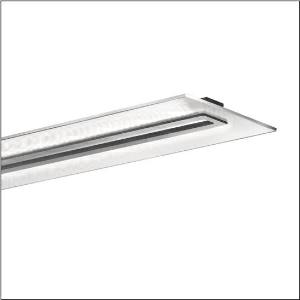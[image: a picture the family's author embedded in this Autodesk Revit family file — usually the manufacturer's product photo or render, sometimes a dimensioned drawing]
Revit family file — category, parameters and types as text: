
# Revit family: vega_r__11_5mn238dlc_e876
name_source: partatom
category: Lighting Fixtures
units: mm (PartAtom-declared; Revit-internal decimal feet)

## family parameters
Cut with Voids When Loaded = No
Host = Face
Light Source = No
Part Type = Normal
Room Calculation Point = No
Round Connector Dimension = Use Diameter
Shared = No

## types (1)
- --- (1 x LED 4000K / CRI = 80 (unbekannt), 4300 lm, 4000K)
    Apparent Load = 31 VA
    CIE Flux Codes = 61 86 97 62 100
    Color Rendering = 80
    Color Temperature = 4000K
    Default Elevation = 1800 mm
    Description = Vega® 11, office luminaire, primary light control with prismatic reflector, of PMMA, transparent prismatic structure, CAT 2 (L<= 1500cd/m²), light emission: direct/indirect distribution, primary light characteristic: symmetric, installation type: suspended mounting, surface-mounted, LED, rated luminous flux: 4.300lm, luminous efficacy: 139lm/W, light colour: 840, colour temperature: 4000K, control gear: ECG, with terminal, 3+2-pole, max. 2.5mm², mains connection: 230V, AC, 50Hz, connection cable inclusive, cable length: 1,5m, rated input power: 31W, luminaire housing, rectangular, rounded, of aluminium section, anodised, metallic grey (RAL 9006), length: 1.250mm, width: 350mm, height: 43mm, luminaire housing, lower part, of aluminium section, anodised, metallic grey (RAL 9006), of PC, grey, protection rating (complete): IP20, insulation class (complete): insulation class I (protective earthing), certification: CE, standard: EN 50419, packaging unit: 1 piece
    Height = 40 mm  [stored 0.131234 ft]
    Lamp = 1 x LED 4000K / CRI >= 80 (unbekannt)
    Lamp Light Flux = 4300 lm
    Lamp count = 1
    Length = 1250 mm
    Luminous efficacy = 139 lm/W
    Manufacturer = Siteco
    ModVariant = No
    Model = 5MN238DLC
    Mounting Place = Ceiling
    Mounting Type = Pendant
    Number of Poles = 1
    OnlyDefault = Yes
    Power Factor = 1
    Product Name = Vega® 11
    Product group = office luminaire | ceiling pendant
    ProductGroupID = 902
    Protection Class = Protection class I
    Protection Degree = IP 20
    RLX_Detail_Level = 1
    RLX_Emergency_Light_Flux = 0 lm
    RLX_Emergency_Type = 0
    RLX_Emergency_Type_DB = No
    RlxData = <blob elided: 62781 chars, md5=000de961>
    Socket = socket
    Standby Power = 0 W
    System Light Flux = 4300 lm
    System Power = 31 W
    Type Comments = factory setting: luminous flux: 100 % | dim-lin: 254 | 231 mA
    Type Image = l_1004807.jpg
    URL = http://relux.com
    VarID = @adj_149717
    Voltage = 0 V
    Weight = 0.00 kg
    Width = 350 mm

note: [stored X ft] marks values corroborated as IEEE doubles in the binary element streams (Revit-internal decimal feet)

## geometry (parser evidence)
native form markers: Blend x4, Sweep x11
no freeform markers — native parametric forms only
